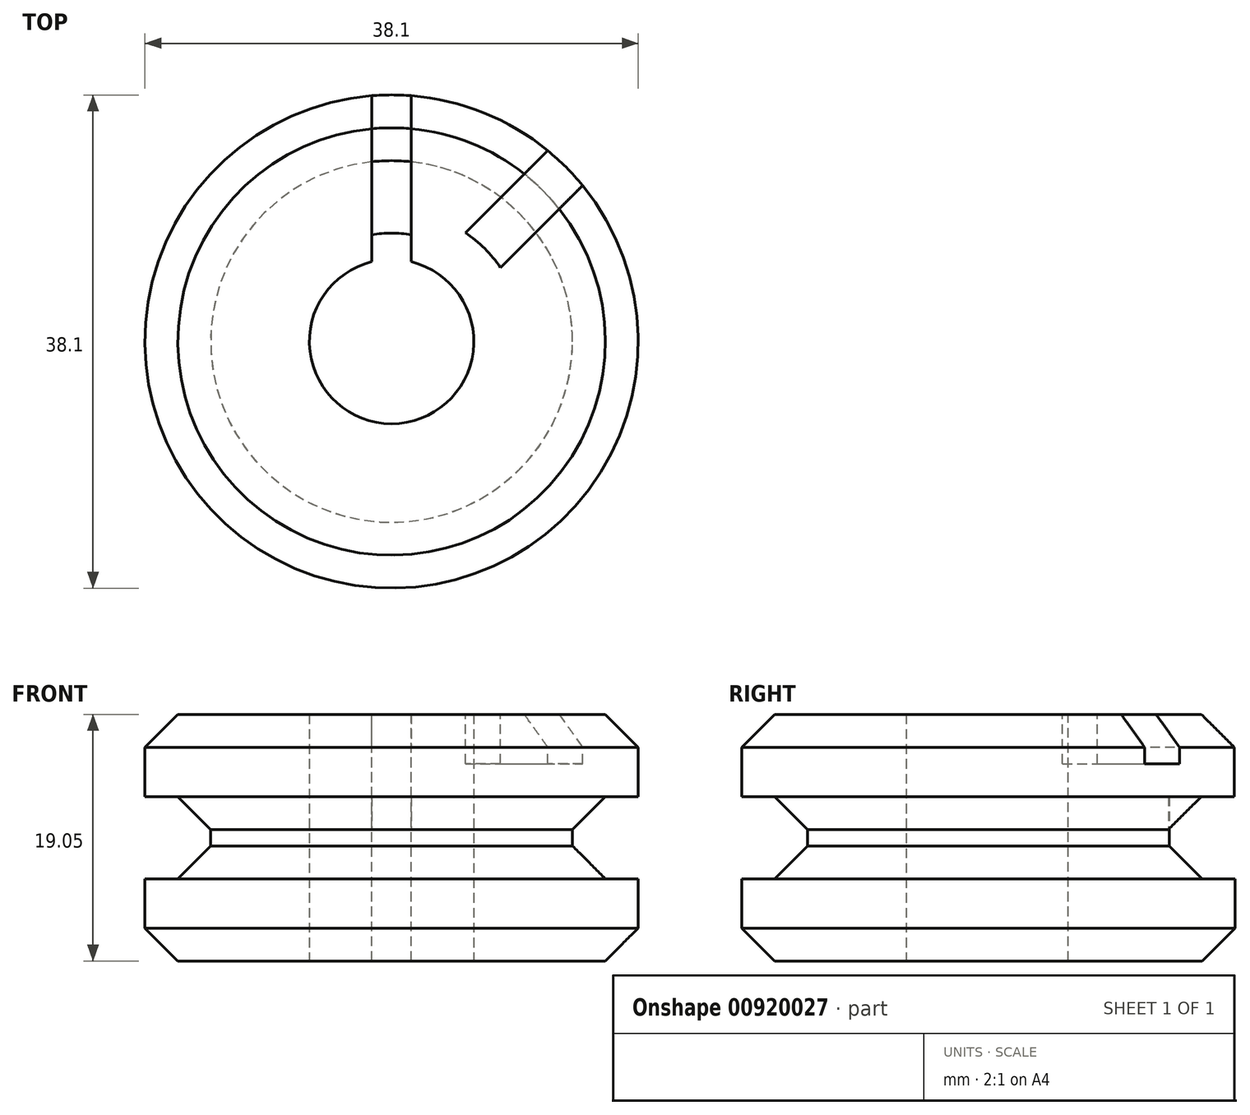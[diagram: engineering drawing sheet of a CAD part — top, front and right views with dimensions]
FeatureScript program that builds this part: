
annotation { "Feature Type Name" : "Feature", "Feature Type Description" : "" }
export const myFeature = defineFeature(function(context is Context, id is Id, definition is map)
    precondition{}
    {
        {
            var Q0;
            Q0=qCreatedBy(makeId("Top.planeOp"),FACE);
            var sketch = newSketch(context, id + "F0", { "sketchPlane" : qUnion([Q0])});
            skCircle(sketch, "E0", {"center": v(0, 0) * mm, "radius": 19.05 * mm});
            skCircle(sketch, "E1", {"center": v(0, 0) * mm, "radius": 6.35 * mm});
            skSolve(sketch);
        }
        {
            var Q0;
            Q0 = qSketchRegion(id + "F0", true);
            extrude(context, id + "F1", {"entities" : qUnion([Q0]), "depth" : 19.05 * mm, "offsetDistance" : 25.4 * mm});
        }
        {
            var Q0;
            Q0=makeQuery(id+"F1.opExtrude","CAP_FACE",FACE,{"disambiguationData":[OSD([sQuery(id+"F0.wireOp",EDGE,"E0"),sQuery(id+"F0.wireOp",EDGE,"E1")])],"isStart":false});
            var sketch = newSketch(context, id + "F2", { "sketchPlane" : qUnion([Q0])});
            skLineSegment(sketch, "E2", {"start": v(-1.52, 18.99) * mm, "end": v(-1.52, 6.16) * mm});
            skLineSegment(sketch, "E3.MirrorCS", {"start": v(1.52, 18.99) * mm, "end": v(1.52, 6.16) * mm});
            skArc(sketch, "E4.0", {"start": v(1.52, 6.16) * mm, "mid": v(0, 6.35) * mm, "end": v(-1.52, 6.16) * mm});
            skArc(sketch, "E5.0", {"start": v(1.52, 18.99) * mm, "mid": v(0, 19.05) * mm, "end": v(-1.52, 18.99) * mm});
            skSolve(sketch);
        }
        {
            var Q0;
            Q0 = qSketchRegion(id + "F2", true);
            extrude(context, id + "F3", {"entities" : qUnion([Q0]), "operationType" : NewBodyOperationType.REMOVE, "oppositeDirection" : true, "depth" : 6.35 * mm, "offsetDistance" : 25.4 * mm});
        }
        {
            var Q0;
            Q0=makeQuery(id+"F3.boolean.opBoolean","COPY",FACE,{"derivedFrom":makeQuery(id+"F3.opExtrude","CAP_FACE",FACE,{"disambiguationData":[OSD([sQuery(id+"F2.wireOp",EDGE,"E2"),sQuery(id+"F2.wireOp",EDGE,"E3.MirrorCS"),sQuery(id+"F2.wireOp",EDGE,"E4.0"),sQuery(id+"F2.wireOp",EDGE,"E5.0")])],"isStart":false})});
            var sketch = newSketch(context, id + "F4", { "sketchPlane" : qUnion([Q0])});
            skArc(sketch, "E6.0", {"start": v(1.52, 6.16) * mm, "mid": v(0, 6.35) * mm, "end": v(-1.52, 6.16) * mm});
            skArc(sketch, "E7.0", {"start": v(1.52, 8.24) * mm, "mid": v(0, 8.38) * mm, "end": v(-1.52, 8.24) * mm});
            skLineSegment(sketch, "E8", {"start": v(-1.52, 8.24) * mm, "end": v(-1.52, 6.16) * mm});
            skLineSegment(sketch, "E9", {"start": v(1.52, 6.16) * mm, "end": v(1.52, 8.24) * mm});
            skSolve(sketch);
        }
        {
            var Q0;
            Q0 = qSketchRegion(id + "F4", true);
            extrude(context, id + "F5", {"entities" : qUnion([Q0]), "operationType" : NewBodyOperationType.REMOVE, "endBound" : BoundingType.UP_TO_NEXT, "oppositeDirection" : true, "depth" : 25.4 * mm, "offsetDistance" : 25.4 * mm});
        }
        {
            var Q0;
            Q0=makeQuery(id+"F1.opExtrude","CAP_FACE",FACE,{"disambiguationData":[OSD([sQuery(id+"F0.wireOp",EDGE,"E0"),sQuery(id+"F0.wireOp",EDGE,"E1")])],"isStart":false});
            var sketch = newSketch(context, id + "F6", { "sketchPlane" : qUnion([Q0])});
            skLineSegment(sketch, "E10", {"start": v(0, 0) * mm, "end": v(13.47, 13.47) * mm, "construction": true});
            skLineSegment(sketch, "E11", {"start": v(5.7, 8.4) * mm, "end": v(12.06, 14.75) * mm});
            skLineSegment(sketch, "E12", {"start": v(8.4, 5.7) * mm, "end": v(14.75, 12.06) * mm});
            skArc(sketch, "E13", {"start": v(5.7, 8.4) * mm, "mid": v(7.18, 7.18) * mm, "end": v(8.4, 5.7) * mm});
            skArc(sketch, "E14", {"start": v(12.06, 14.75) * mm, "mid": v(13.47, 13.47) * mm, "end": v(14.75, 12.06) * mm});
            skSolve(sketch);
        }
        {
            var Q0;
            Q0 = qSketchRegion(id + "F6", true);
            extrude(context, id + "F7", {"entities" : qUnion([Q0]), "operationType" : NewBodyOperationType.REMOVE, "oppositeDirection" : true, "depth" : 3.8 * mm, "offsetDistance" : 25.4 * mm});
        }
        {
            var Q0;
            Q0=qCreatedBy(makeId("Top.planeOp"),FACE);
            cPlane(context, id + "F8", {"entities" : qUnion([Q0]), "cplaneType" : CPlaneType.OFFSET, "offset" : 6.35 * mm, "width" : 152.4 * mm, "height" : 152.4 * mm});
        }
        {
            var Q0;
            Q0=qCreatedBy(id+"F8.planeOp",FACE);
            var sketch = newSketch(context, id + "F9", { "sketchPlane" : qUnion([Q0])});
            skCircle(sketch, "E15", {"center": v(0, 0) * mm, "radius": 13.97 * mm});
            skCircle(sketch, "E16.0", {"center": v(0, 0) * mm, "radius": 19.05 * mm});
            skSolve(sketch);
        }
        {
            var Q0;
            Q0 = qSketchRegion(id + "F9", true);
            var Q1;
            Q1=makeQuery(id+"F3.boolean.opBoolean","COPY",FACE,{"derivedFrom":makeQuery(id+"F3.opExtrude","CAP_FACE",FACE,{"disambiguationData":[OSD([sQuery(id+"F2.wireOp",EDGE,"E2"),sQuery(id+"F2.wireOp",EDGE,"E3.MirrorCS"),sQuery(id+"F2.wireOp",EDGE,"E4.0"),sQuery(id+"F2.wireOp",EDGE,"E5.0")])],"isStart":false})});
            extrude(context, id + "F10", {"entities" : qUnion([Q0]), "operationType" : NewBodyOperationType.REMOVE, "endBound" : BoundingType.UP_TO_SURFACE, "depth" : 7.62 * mm, "endBoundEntityFace" : qUnion([Q1]), "offsetDistance" : 25.4 * mm});
        }
        {
            var Q0;
            Q0=makeQuery(id+"F10.boolean.opBoolean","COPY",EDGE,{"derivedFrom":makeQuery(id+"F10.opExtrude","CAP_EDGE",EDGE,{"disambiguationData":[OSD([sQuery(id+"F9.wireOp",EDGE,"E15")])],"isStart":true})});
            var Q1;
            {var subQ0=sQuery(id+"F9.wireOp",EDGE,"E15");Q1=makeQuery(id+"F10.boolean.opBoolean","COPY",EDGE,{"disambiguationData":[topologyDisambiguationEdgeConnected([makeQuery(id+"F10.opExtrude","CAP_FACE",FACE,{"disambiguationData":[OSD([subQ0,sQuery(id+"F9.wireOp",EDGE,"E16.0")])],"isStart":false})])],"derivedFrom":makeQuery(id+"F10.opExtrude","CAP_EDGE",EDGE,{"disambiguationData":[OSD([subQ0])],"isStart":false})});}
            chamfer(context, id + "F11", {"entities" : qUnion([Q0, Q1]), "width" : 2.54 * mm, "tangentPropagation" : true});
        }
        {
            var Q0;
            Q0=makeQuery(id+"F1.opExtrude","CAP_EDGE",EDGE,{"disambiguationData":[OSD([sQuery(id+"F0.wireOp",EDGE,"E0")])],"isStart":true});
            chamfer(context, id + "F12", {"entities" : qUnion([Q0]), "width" : 2.54 * mm, "tangentPropagation" : true});
        }
        {
            var Q0;
            {var subQ0=sQuery(id+"F0.wireOp",EDGE,"E0");var subQ3=sQuery(id+"F6.wireOp",EDGE,"E12");var subQ4=makeQuery(id+"FPUyBDiLou1EtBU_1.1.F7.opExtrude","SWEPT_FACE",FACE,{"disambiguationData":[OSD([subQ3])]});var subQ5=makeQuery(id+"F3.boolean.opBoolean","COPY",FACE,{"derivedFrom":makeQuery(id+"F3.opExtrude","SWEPT_FACE",FACE,{"disambiguationData":[OSD([sQuery(id+"F2.wireOp",EDGE,"E2")])]})});Q0=makeQuery(id+"FPUyBDiLou1EtBU_1.2.F7.boolean.opBoolean","SPLIT",EDGE,{"disambiguationData":[TD([makeQuery(id+"FPUyBDiLou1EtBU_1.1.F7.boolean.opBoolean","COPY",FACE,{"derivedFrom":subQ4})])],"derivedFrom":makeQuery(id+"FPUyBDiLou1EtBU_1.1.F7.boolean.opBoolean","SPLIT",EDGE,{"disambiguationData":[TD([subQ5])],"derivedFrom":makeQuery(id+"F7.boolean.opBoolean","SPLIT",EDGE,{"disambiguationData":[TD([subQ5])],"derivedFrom":makeQuery(id+"F1.opExtrude","CAP_EDGE",EDGE,{"disambiguationData":[OSD([subQ0])],"isStart":false})})})});}
            var Q1;
            {var subQ0=sQuery(id+"F0.wireOp",EDGE,"E0");var subQ3=sQuery(id+"F6.wireOp",EDGE,"E12");var subQ4=makeQuery(id+"FPUyBDiLou1EtBU_1.2.F7.opExtrude","SWEPT_FACE",FACE,{"disambiguationData":[OSD([subQ3])]});var subQ5=makeQuery(id+"F3.boolean.opBoolean","COPY",FACE,{"derivedFrom":makeQuery(id+"F3.opExtrude","SWEPT_FACE",FACE,{"disambiguationData":[OSD([sQuery(id+"F2.wireOp",EDGE,"E2")])]})});Q1=makeQuery(id+"FPUyBDiLou1EtBU_1.3.F7.boolean.opBoolean","SPLIT",EDGE,{"disambiguationData":[TD([makeQuery(id+"FPUyBDiLou1EtBU_1.2.F7.boolean.opBoolean","COPY",FACE,{"derivedFrom":subQ4})])],"derivedFrom":makeQuery(id+"FPUyBDiLou1EtBU_1.2.F7.boolean.opBoolean","SPLIT",EDGE,{"disambiguationData":[TD([subQ5])],"derivedFrom":makeQuery(id+"FPUyBDiLou1EtBU_1.1.F7.boolean.opBoolean","SPLIT",EDGE,{"disambiguationData":[TD([subQ5])],"derivedFrom":makeQuery(id+"F7.boolean.opBoolean","SPLIT",EDGE,{"disambiguationData":[TD([subQ5])],"derivedFrom":makeQuery(id+"F1.opExtrude","CAP_EDGE",EDGE,{"disambiguationData":[OSD([subQ0])],"isStart":false})})})})});}
            var Q2;
            {var subQ0=sQuery(id+"F0.wireOp",EDGE,"E0");var subQ2=sQuery(id+"F6.wireOp",EDGE,"E12");var subQ3=makeQuery(id+"FPUyBDiLou1EtBU_1.3.F7.opExtrude","SWEPT_FACE",FACE,{"disambiguationData":[OSD([subQ2])]});var subQ5=makeQuery(id+"F3.boolean.opBoolean","COPY",FACE,{"derivedFrom":makeQuery(id+"F3.opExtrude","SWEPT_FACE",FACE,{"disambiguationData":[OSD([sQuery(id+"F2.wireOp",EDGE,"E2")])]})});Q2=makeQuery(id+"FPUyBDiLou1EtBU_1.4.F7.boolean.opBoolean","SPLIT",EDGE,{"disambiguationData":[TD([makeQuery(id+"FPUyBDiLou1EtBU_1.3.F7.boolean.opBoolean","COPY",FACE,{"derivedFrom":subQ3})])],"derivedFrom":makeQuery(id+"FPUyBDiLou1EtBU_1.3.F7.boolean.opBoolean","SPLIT",EDGE,{"disambiguationData":[TD([subQ5])],"derivedFrom":makeQuery(id+"FPUyBDiLou1EtBU_1.2.F7.boolean.opBoolean","SPLIT",EDGE,{"disambiguationData":[TD([subQ5])],"derivedFrom":makeQuery(id+"FPUyBDiLou1EtBU_1.1.F7.boolean.opBoolean","SPLIT",EDGE,{"disambiguationData":[TD([subQ5])],"derivedFrom":makeQuery(id+"F7.boolean.opBoolean","SPLIT",EDGE,{"disambiguationData":[TD([subQ5])],"derivedFrom":makeQuery(id+"F1.opExtrude","CAP_EDGE",EDGE,{"disambiguationData":[OSD([subQ0])],"isStart":false})})})})})});}
            var Q3;
            {var subQ0=sQuery(id+"F0.wireOp",EDGE,"E0");var subQ3=sQuery(id+"F6.wireOp",EDGE,"E12");var subQ4=makeQuery(id+"FPUyBDiLou1EtBU_1.4.F7.opExtrude","SWEPT_FACE",FACE,{"disambiguationData":[OSD([subQ3])]});var subQ5=makeQuery(id+"F3.boolean.opBoolean","COPY",FACE,{"derivedFrom":makeQuery(id+"F3.opExtrude","SWEPT_FACE",FACE,{"disambiguationData":[OSD([sQuery(id+"F2.wireOp",EDGE,"E2")])]})});Q3=makeQuery(id+"FPUyBDiLou1EtBU_1.5.F7.boolean.opBoolean","SPLIT",EDGE,{"disambiguationData":[TD([makeQuery(id+"FPUyBDiLou1EtBU_1.4.F7.boolean.opBoolean","COPY",FACE,{"derivedFrom":subQ4})])],"derivedFrom":makeQuery(id+"FPUyBDiLou1EtBU_1.4.F7.boolean.opBoolean","SPLIT",EDGE,{"disambiguationData":[TD([subQ5])],"derivedFrom":makeQuery(id+"FPUyBDiLou1EtBU_1.3.F7.boolean.opBoolean","SPLIT",EDGE,{"disambiguationData":[TD([subQ5])],"derivedFrom":makeQuery(id+"FPUyBDiLou1EtBU_1.2.F7.boolean.opBoolean","SPLIT",EDGE,{"disambiguationData":[TD([subQ5])],"derivedFrom":makeQuery(id+"FPUyBDiLou1EtBU_1.1.F7.boolean.opBoolean","SPLIT",EDGE,{"disambiguationData":[TD([subQ5])],"derivedFrom":makeQuery(id+"F7.boolean.opBoolean","SPLIT",EDGE,{"disambiguationData":[TD([subQ5])],"derivedFrom":makeQuery(id+"F1.opExtrude","CAP_EDGE",EDGE,{"disambiguationData":[OSD([subQ0])],"isStart":false})})})})})})});}
            var Q4;
            {var subQ0=sQuery(id+"F0.wireOp",EDGE,"E0");var subQ3=sQuery(id+"F6.wireOp",EDGE,"E12");var subQ4=makeQuery(id+"FPUyBDiLou1EtBU_1.5.F7.opExtrude","SWEPT_FACE",FACE,{"disambiguationData":[OSD([subQ3])]});var subQ5=makeQuery(id+"F3.boolean.opBoolean","COPY",FACE,{"derivedFrom":makeQuery(id+"F3.opExtrude","SWEPT_FACE",FACE,{"disambiguationData":[OSD([sQuery(id+"F2.wireOp",EDGE,"E2")])]})});Q4=makeQuery(id+"FPUyBDiLou1EtBU_1.6.F7.boolean.opBoolean","SPLIT",EDGE,{"disambiguationData":[TD([makeQuery(id+"FPUyBDiLou1EtBU_1.5.F7.boolean.opBoolean","COPY",FACE,{"derivedFrom":subQ4})])],"derivedFrom":makeQuery(id+"FPUyBDiLou1EtBU_1.5.F7.boolean.opBoolean","SPLIT",EDGE,{"disambiguationData":[TD([subQ5])],"derivedFrom":makeQuery(id+"FPUyBDiLou1EtBU_1.4.F7.boolean.opBoolean","SPLIT",EDGE,{"disambiguationData":[TD([subQ5])],"derivedFrom":makeQuery(id+"FPUyBDiLou1EtBU_1.3.F7.boolean.opBoolean","SPLIT",EDGE,{"disambiguationData":[TD([subQ5])],"derivedFrom":makeQuery(id+"FPUyBDiLou1EtBU_1.2.F7.boolean.opBoolean","SPLIT",EDGE,{"disambiguationData":[TD([subQ5])],"derivedFrom":makeQuery(id+"FPUyBDiLou1EtBU_1.1.F7.boolean.opBoolean","SPLIT",EDGE,{"disambiguationData":[TD([subQ5])],"derivedFrom":makeQuery(id+"F7.boolean.opBoolean","SPLIT",EDGE,{"disambiguationData":[TD([subQ5])],"derivedFrom":makeQuery(id+"F1.opExtrude","CAP_EDGE",EDGE,{"disambiguationData":[OSD([subQ0])],"isStart":false})})})})})})})});}
            var Q5;
            {var subQ0=sQuery(id+"F0.wireOp",EDGE,"E0");var subQ3=makeQuery(id+"F3.boolean.opBoolean","COPY",FACE,{"derivedFrom":makeQuery(id+"F3.opExtrude","SWEPT_FACE",FACE,{"disambiguationData":[OSD([sQuery(id+"F2.wireOp",EDGE,"E2")])]})});Q5=makeQuery(id+"FPUyBDiLou1EtBU_1.6.F7.boolean.opBoolean","SPLIT",EDGE,{"disambiguationData":[TD([subQ3])],"derivedFrom":makeQuery(id+"FPUyBDiLou1EtBU_1.5.F7.boolean.opBoolean","SPLIT",EDGE,{"disambiguationData":[TD([subQ3])],"derivedFrom":makeQuery(id+"FPUyBDiLou1EtBU_1.4.F7.boolean.opBoolean","SPLIT",EDGE,{"disambiguationData":[TD([subQ3])],"derivedFrom":makeQuery(id+"FPUyBDiLou1EtBU_1.3.F7.boolean.opBoolean","SPLIT",EDGE,{"disambiguationData":[TD([subQ3])],"derivedFrom":makeQuery(id+"FPUyBDiLou1EtBU_1.2.F7.boolean.opBoolean","SPLIT",EDGE,{"disambiguationData":[TD([subQ3])],"derivedFrom":makeQuery(id+"FPUyBDiLou1EtBU_1.1.F7.boolean.opBoolean","SPLIT",EDGE,{"disambiguationData":[TD([subQ3])],"derivedFrom":makeQuery(id+"F7.boolean.opBoolean","SPLIT",EDGE,{"disambiguationData":[TD([subQ3])],"derivedFrom":makeQuery(id+"F1.opExtrude","CAP_EDGE",EDGE,{"disambiguationData":[OSD([subQ0])],"isStart":false})})})})})})})});}
            var Q6;
            {var subQ0=sQuery(id+"F0.wireOp",EDGE,"E0");Q6=makeQuery(id+"F7.boolean.opBoolean","SPLIT",EDGE,{"disambiguationData":[TD([makeQuery(id+"F3.boolean.opBoolean","COPY",FACE,{"derivedFrom":makeQuery(id+"F3.opExtrude","SWEPT_FACE",FACE,{"disambiguationData":[OSD([sQuery(id+"F2.wireOp",EDGE,"E3.MirrorCS")])]})})])],"derivedFrom":makeQuery(id+"F1.opExtrude","CAP_EDGE",EDGE,{"disambiguationData":[OSD([subQ0])],"isStart":false})});}
            var Q7;
            {var subQ0=sQuery(id+"F0.wireOp",EDGE,"E0");var subQ3=makeQuery(id+"F7.opExtrude","SWEPT_FACE",FACE,{"disambiguationData":[OSD([sQuery(id+"F6.wireOp",EDGE,"E12")])]});Q7=makeQuery(id+"FPUyBDiLou1EtBU_1.1.F7.boolean.opBoolean","SPLIT",EDGE,{"disambiguationData":[TD([makeQuery(id+"F7.boolean.opBoolean","COPY",FACE,{"derivedFrom":subQ3})])],"derivedFrom":makeQuery(id+"F7.boolean.opBoolean","SPLIT",EDGE,{"disambiguationData":[TD([makeQuery(id+"F3.boolean.opBoolean","COPY",FACE,{"derivedFrom":makeQuery(id+"F3.opExtrude","SWEPT_FACE",FACE,{"disambiguationData":[OSD([sQuery(id+"F2.wireOp",EDGE,"E2")])]})})])],"derivedFrom":makeQuery(id+"F1.opExtrude","CAP_EDGE",EDGE,{"disambiguationData":[OSD([subQ0])],"isStart":false})})});}
            chamfer(context, id + "F13", {"entities" : qUnion([Q0, Q1, Q2, Q3, Q4, Q5, Q6, Q7]), "width" : 2.54 * mm, "tangentPropagation" : true});
        }
    });
